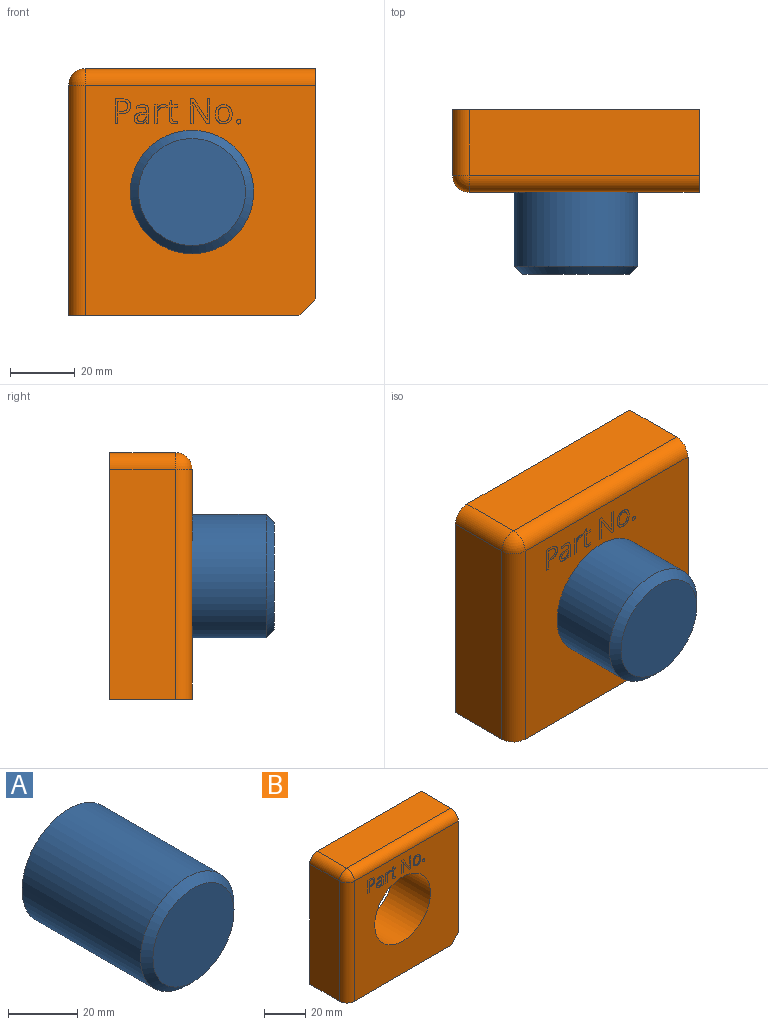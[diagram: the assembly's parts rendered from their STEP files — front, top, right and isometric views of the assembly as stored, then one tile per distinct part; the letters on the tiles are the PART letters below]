
ASSEMBLY  parts=2 mates=1
PART A: 4 faces, bbox 38.1x50.8x38.1 mm
  f0: cylinder r=19.05mm len=48.26mm, axis (0,1,0), area 5776.5mm2, adj f2,f3
  f1: plane 33.02x33.02mm, normal (0,-1,0), area 856.3mm2, adj f3
  f2: plane 38.1x38.1mm, normal (0,1,0), area 1140.1mm2, adj f0
  f3: cone r=16.51mm half-angle=45deg, axis (0,1,0), area 401.3mm2, adj f0,f1
PART B: 22 faces, bbox 76.2x25.4x76.2 mm
  f0: plane 71.12x71.12mm, normal (0,-1,0), area 3803.1mm2, adj f2,f3,f4,f5,f7,f9,f12,f13
  f1: plane 4.47x3.46mm, normal (0,-1,0), area 12.8mm2, adj f3
  f2: plane 1.42x1.26mm, normal (0,-1,0), area 1.5mm2, adj f0
  f3: plane 5.93x5.26mm, normal (0,-1,0), area 12.6mm2, adj f0,f1
  f4: plane 7.63x5.96mm, normal (0,-1,0), area 19.2mm2, adj f0
  f5: plane 7.16x3.39mm, normal (0,-1,0), area 8.5mm2, adj f0
  f6: plane 2.81x2.2mm, normal (0,-1,0), area 5mm2, adj f9
  f7: plane 5.83x3.3mm, normal (0,-1,0), area 6.8mm2, adj f0
  f8: plane 3.1x3.03mm, normal (0,-1,0), area 8.4mm2, adj f14
  f9: plane 5.92x4.59mm, normal (0,-1,0), area 12.8mm2, adj f0,f6
  f10: plane 71.12x20.32mm, normal (0,0,1), area 1445.2mm2, adj f13,f15,f17,f20
  f11: plane 71.12x20.32mm, normal (-1,0,0), area 1445.2mm2, adj f12,f15,f18,f20
  f12: plane 71.12x25.4mm, normal (0,0,-1), area 1800.9mm2, adj f0,f11,f15,f18,f21
  f13: plane 71.12x25.4mm, normal (1,0,0), area 1800.9mm2, adj f0,f10,f15,f17,f21
  f14: plane 7.63x4.84mm, normal (0,-1,0), area 14.4mm2, adj f0,f8
  f15: plane 76.2x76.2mm, normal (0,1,0), area 4647.9mm2, adj f10,f11,f12,f13,f16,f20,f21
  f16: cylinder r=19.05mm len=38.1mm, axis (0,1,0), area 3040.2mm2, adj f0,f15
  f17: cylinder r=5.08mm len=71.12mm, axis (1,0,0), area 567.5mm2, adj f0,f10,f13,f19
  f18: cylinder r=5.08mm len=71.12mm, axis (0,0,1), area 567.5mm2, adj f0,f11,f12,f19
  f19: sphere r=5.08mm, area 40.5mm2, adj f17,f18,f20
  f20: cylinder r=5.08mm len=20.32mm, axis (0,-1,0), area 162.1mm2, adj f10,f11,f15,f19
  f21: plane 25.4x5.08mm, normal (0.71,0,-0.71), area 182.5mm2, adj f0,f12,f13,f15
PLACE A t=(24.73,40.5,13.49)mm
PLACE B t=(24.73,27.8,13.49)mm
MATE fastened A.f0 <-> B.f16  axis (0,1,0) through (24.73,40.5,13.49)mm
